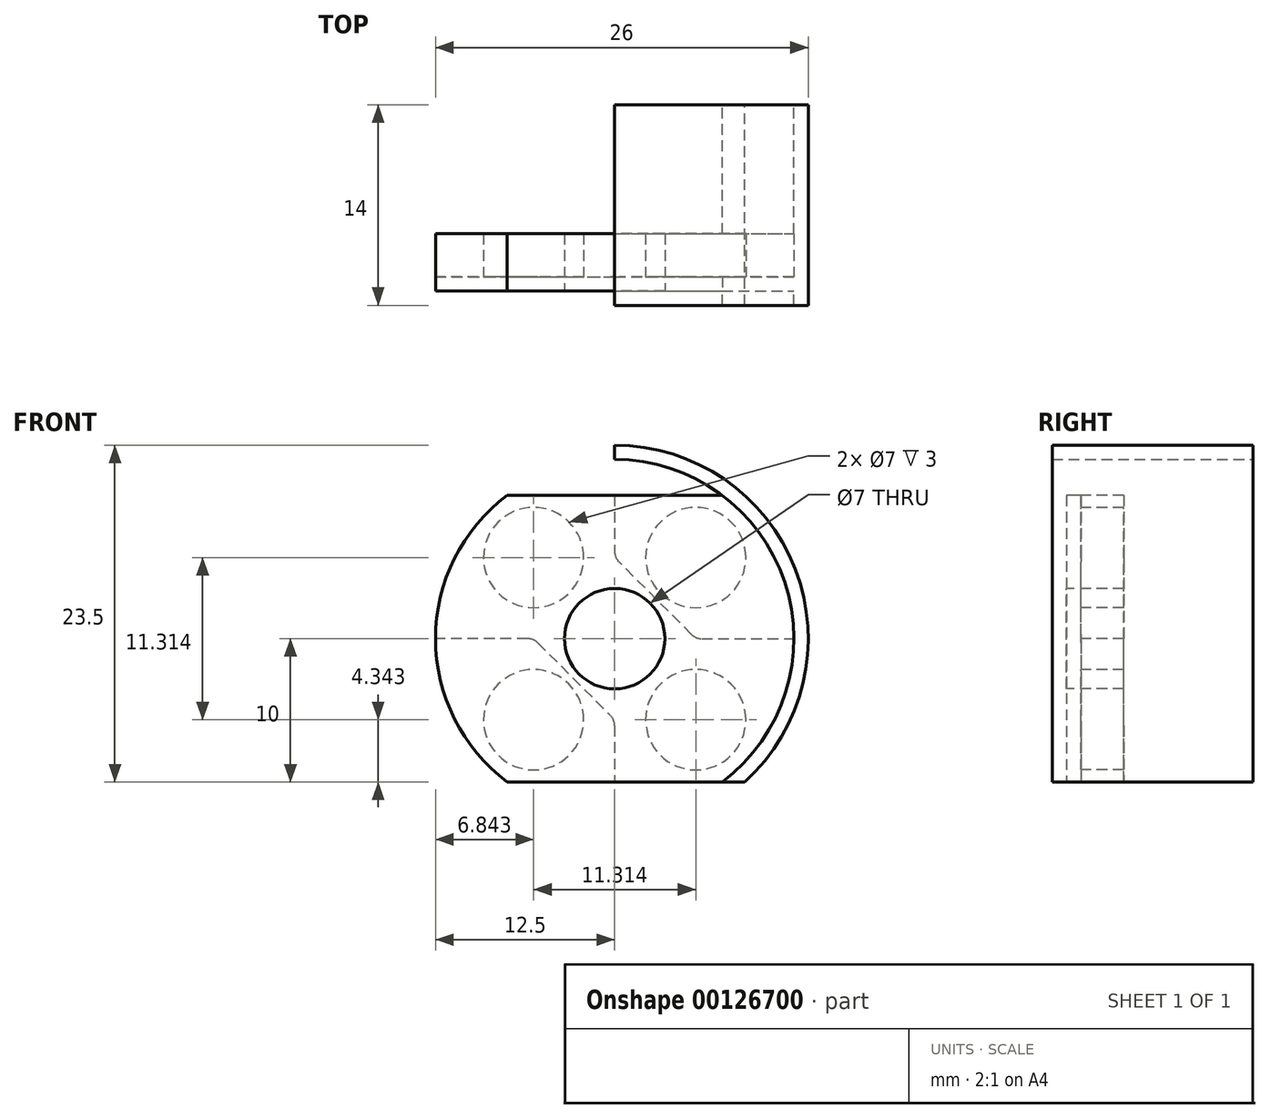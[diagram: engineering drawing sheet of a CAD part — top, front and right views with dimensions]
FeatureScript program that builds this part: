
annotation { "Feature Type Name" : "Feature", "Feature Type Description" : "" }
export const myFeature = defineFeature(function(context is Context, id is Id, definition is map)
    precondition{}
    {
        {
            var Q0;
            Q0=qCreatedBy(makeId("Front.planeOp"),FACE);
            var sketch = newSketch(context, id + "F0", { "sketchPlane" : qUnion([Q0])});
            skCircle(sketch, "E0", {"center": v(0, 0) * mm, "radius": 13.5 * mm});
            skLineSegment(sketch, "E1", {"start": v(0, 13.5) * mm, "end": v(0, 6.07) * mm});
            skLineSegment(sketch, "E2", {"start": v(6.07, 0) * mm, "end": v(13.5, 0) * mm});
            skCircle(sketch, "E3.0", {"center": v(0, 0) * mm, "radius": 12.5 * mm});
            skLineSegment(sketch, "E4", {"start": v(-8.84, 8.84) * mm, "end": v(8.84, -8.84) * mm});
            skCircle(sketch, "E5", {"center": v(0, 0) * mm, "radius": 3.5 * mm});
            skCircle(sketch, "E6", {"center": v(-5.66, 5.66) * mm, "radius": 3.5 * mm});
            skCircle(sketch, "E7", {"center": v(5.66, -5.66) * mm, "radius": 3.5 * mm});
            skCircle(sketch, "E8.MirrorC", {"center": v(5.66, 5.66) * mm, "radius": 3.5 * mm});
            skCircle(sketch, "E9.MirrorC", {"center": v(-5.66, -5.66) * mm, "radius": 3.5 * mm});
            skPoint(sketch, "E10", {"position": v(-2.83, 2.83) * mm});
            skLineSegment(sketch, "E11", {"start": v(-0.3, 5.36) * mm, "end": v(-5.36, 0.3) * mm});
            skLineSegment(sketch, "E12.MirrorCS", {"start": v(0.3, 5.36) * mm, "end": v(5.36, 0.3) * mm});
            skLineSegment(sketch, "E13.MirrorCS", {"start": v(0.3, -5.36) * mm, "end": v(5.36, -0.3) * mm});
            skLineSegment(sketch, "E14.MirrorCS", {"start": v(-0.3, -5.36) * mm, "end": v(-5.36, -0.3) * mm});
            skPoint(sketch, "E15.newPointA", {"position": v(0, 5.66) * mm});
            skArc(sketch, "E15.filletArc", {"start": v(-0.3, 5.36) * mm, "mid": v(-0.08, 5.69) * mm, "end": v(0, 6.07) * mm});
            skArc(sketch, "E16.filletArc", {"start": v(0, 6.07) * mm, "mid": v(0.08, 5.69) * mm, "end": v(0.3, 5.36) * mm});
            skPoint(sketch, "E17.newPointA", {"position": v(-13.5, 0) * mm});
            skPoint(sketch, "E17.newPointB", {"position": v(5.66, 0) * mm});
            skArc(sketch, "E17.filletArc", {"start": v(5.36, 0.3) * mm, "mid": v(5.69, 0.08) * mm, "end": v(6.07, 0) * mm});
            skArc(sketch, "E18.filletArc", {"start": v(6.07, 0) * mm, "mid": v(5.69, -0.08) * mm, "end": v(5.36, -0.3) * mm});
            skLineSegment(sketch, "E19", {"start": v(0, -6.07) * mm, "end": v(0, -12.5) * mm});
            skLineSegment(sketch, "E20", {"start": v(-6.07, 0) * mm, "end": v(-12.5, 0) * mm});
            skPoint(sketch, "E21.visualSharp", {"position": v(0, -5.66) * mm});
            skArc(sketch, "E21.filletArc", {"start": v(0.3, -5.36) * mm, "mid": v(0.08, -5.69) * mm, "end": v(0, -6.07) * mm});
            skArc(sketch, "E22.filletArc", {"start": v(0, -6.07) * mm, "mid": v(-0.08, -5.69) * mm, "end": v(-0.3, -5.36) * mm});
            skPoint(sketch, "E23.visualSharp", {"position": v(-5.66, 0) * mm});
            skArc(sketch, "E23.filletArc", {"start": v(-5.36, -0.3) * mm, "mid": v(-5.69, -0.08) * mm, "end": v(-6.07, 0) * mm});
            skArc(sketch, "E24.filletArc", {"start": v(-6.07, 0) * mm, "mid": v(-5.69, 0.08) * mm, "end": v(-5.36, 0.3) * mm});
            skLineSegment(sketch, "E25", {"start": v(-9.07, 10) * mm, "end": v(9.07, 10) * mm});
            skLineSegment(sketch, "E26", {"start": v(-9.07, -10) * mm, "end": v(9.07, -10) * mm});
            skSolve(sketch);
        }
        {
            var Q0;
            Q0=makeQuery(id+"F2.opExtrude","CAP_FACE",FACE,{"disambiguationData":[OSD([sQuery(id+"F0.wireOp",EDGE,"E0"),sQuery(id+"F0.wireOp",EDGE,"E3.0"),sQuery(id+"F0.wireOp",EDGE,"E25")])],"isStart":false});
            var Q1;
            {var subQ5=sQuery(id+"F0.wireOp",EDGE,"E15.filletArc");Q1=makeQuery(id+"F0.imprint","IMPRINT",FACE,{"disambiguationData":[TD([[makeQuery(id+"F0.imprint","IMPRINT",EDGE,{"derivedFrom":subQ5}),1.0]])]});}
            var Q2;
            Q2=makeQuery(id+"F0.imprint","IMPRINT",FACE,{"disambiguationData":[TD([[makeQuery(id+"F0.imprint","IMPRINT",EDGE,{"derivedFrom":sQuery(id+"F0.wireOp",EDGE,"E12.MirrorCS")}),-1.0]])]});
            var Q3;
            Q3=makeQuery(id+"F0.imprint","IMPRINT",FACE,{"disambiguationData":[TD([[makeQuery(id+"F0.imprint","IMPRINT",EDGE,{"derivedFrom":sQuery(id+"F0.wireOp",EDGE,"E14.MirrorCS")}),-1.0]])]});
            var Q4;
            Q4=makeQuery(id+"F0.imprint","IMPRINT",FACE,{"disambiguationData":[TD([[makeQuery(id+"F0.imprint","IMPRINT",EDGE,{"derivedFrom":sQuery(id+"F0.wireOp",EDGE,"E9.MirrorC")}),1.0]])]});
            var Q5;
            {var subQ10=sQuery(id+"F0.wireOp",EDGE,"E18.filletArc");Q5=makeQuery(id+"F0.imprint","IMPRINT",FACE,{"disambiguationData":[TD([[makeQuery(id+"F0.imprint","IMPRINT",EDGE,{"derivedFrom":subQ10}),1.0]])]});}
            var Q6;
            {var subQ12=sQuery(id+"F0.wireOp",EDGE,"E21.filletArc");Q6=makeQuery(id+"F0.imprint","IMPRINT",FACE,{"disambiguationData":[TD([[makeQuery(id+"F0.imprint","IMPRINT",EDGE,{"derivedFrom":subQ12}),1.0]])]});}
            var Q7;
            Q7=makeQuery(id+"F0.imprint","IMPRINT",FACE,{"disambiguationData":[TD([[makeQuery(id+"F0.imprint","IMPRINT",EDGE,{"derivedFrom":sQuery(id+"F0.wireOp",EDGE,"E8.MirrorC")}),1.0]])]});
            var Q8;
            {var subQ9=sQuery(id+"F0.wireOp",EDGE,"E20");Q8=makeQuery(id+"F0.imprint","IMPRINT",FACE,{"disambiguationData":[TD([[makeQuery(id+"F0.imprint","IMPRINT",EDGE,{"derivedFrom":subQ9}),-1.0]])]});}
            extrude(context, id + "F1", {"entities" : qUnion([Q0, Q1, Q2, Q3, Q4, Q5, Q6, Q7, Q8]), "oppositeDirection" : true, "depth" : 4 * mm});
        }
        {
            var Q0;
            {var subQ10=sQuery(id+"F0.wireOp",EDGE,"E2");var subQ11=sQuery(id+"F0.wireOp",EDGE,"E0");var subQ12=makeQuery(id+"F0.imprint","INTERSECT",VERTEX,{"derivedFrom":[subQ11,subQ10]});Q0=makeQuery(id+"F0.imprint","IMPRINT",FACE,{"disambiguationData":[TD([[makeQuery(id+"F0.imprint","IMPRINT",EDGE,{"disambiguationData":[TD([[subQ12,1.0]])],"derivedFrom":subQ11}),1.0]])]});}
            var Q1;
            {var subQ0=sQuery(id+"F0.wireOp",EDGE,"E2");var subQ1=sQuery(id+"F0.wireOp",EDGE,"E0");var subQ2=makeQuery(id+"F0.imprint","INTERSECT",VERTEX,{"derivedFrom":[subQ1,subQ0]});Q1=makeQuery(id+"F0.imprint","IMPRINT",FACE,{"disambiguationData":[TD([[makeQuery(id+"F0.imprint","IMPRINT",EDGE,{"disambiguationData":[TD([[subQ2,-1.0]])],"derivedFrom":subQ1}),1.0]])]});}
            var Q2;
            {var subQ3=sQuery(id+"F0.wireOp",EDGE,"E25");var subQ7=sQuery(id+"F0.wireOp",EDGE,"E0");var subQ8=makeQuery(id+"F0.imprint","INTERSECT",VERTEX,{"disambiguationData":[OD(0.0)],"derivedFrom":[subQ7,subQ3]});Q2=makeQuery(id+"F0.imprint","IMPRINT",FACE,{"disambiguationData":[TD([[makeQuery(id+"F0.imprint","IMPRINT",EDGE,{"disambiguationData":[TD([[subQ8,-1.0]])],"derivedFrom":subQ7}),1.0]])]});}
            extrude(context, id + "F2", {"entities" : qUnion([Q0, Q1, Q2]), "operationType" : NewBodyOperationType.ADD, "depth" : 1 * mm});
        }
        {
            var Q0;
            {var subQ0=sQuery(id+"F0.wireOp",EDGE,"E6");var subQ1=sQuery(id+"F0.wireOp",EDGE,"E4");var subQ2=makeQuery(id+"F0.imprint","INTERSECT",VERTEX,{"disambiguationData":[OD(0.0)],"derivedFrom":[subQ1,subQ0]});Q0=makeQuery(id+"F0.imprint","IMPRINT",FACE,{"disambiguationData":[TD([[makeQuery(id+"F0.imprint","IMPRINT",EDGE,{"disambiguationData":[TD([[subQ2,-1.0]])],"derivedFrom":subQ1}),-1.0]])]});}
            var Q1;
            {var subQ0=sQuery(id+"F0.wireOp",EDGE,"E6");var subQ1=sQuery(id+"F0.wireOp",EDGE,"E4");var subQ2=makeQuery(id+"F0.imprint","INTERSECT",VERTEX,{"disambiguationData":[OD(0.0)],"derivedFrom":[subQ1,subQ0]});Q1=makeQuery(id+"F0.imprint","IMPRINT",FACE,{"disambiguationData":[TD([[makeQuery(id+"F0.imprint","IMPRINT",EDGE,{"disambiguationData":[TD([[subQ2,-1.0]])],"derivedFrom":subQ1}),1.0]])]});}
            var Q2;
            Q2=makeQuery(id+"F0.imprint","IMPRINT",FACE,{"disambiguationData":[TD([[makeQuery(id+"F0.imprint","IMPRINT",EDGE,{"derivedFrom":sQuery(id+"F0.wireOp",EDGE,"E8.MirrorC")}),-1.0]])]});
            var Q3;
            {var subQ0=sQuery(id+"F0.wireOp",EDGE,"E5");var subQ1=sQuery(id+"F0.wireOp",EDGE,"E4");var subQ2=makeQuery(id+"F0.imprint","INTERSECT",VERTEX,{"disambiguationData":[OD(0.0)],"derivedFrom":[subQ1,subQ0]});Q3=makeQuery(id+"F0.imprint","IMPRINT",FACE,{"disambiguationData":[TD([[makeQuery(id+"F0.imprint","IMPRINT",EDGE,{"disambiguationData":[TD([[subQ2,-1.0]])],"derivedFrom":subQ1}),1.0]])]});}
            var Q4;
            {var subQ0=sQuery(id+"F0.wireOp",EDGE,"E5");var subQ1=sQuery(id+"F0.wireOp",EDGE,"E4");var subQ2=makeQuery(id+"F0.imprint","INTERSECT",VERTEX,{"disambiguationData":[OD(0.0)],"derivedFrom":[subQ1,subQ0]});Q4=makeQuery(id+"F0.imprint","IMPRINT",FACE,{"disambiguationData":[TD([[makeQuery(id+"F0.imprint","IMPRINT",EDGE,{"disambiguationData":[TD([[subQ2,-1.0]])],"derivedFrom":subQ1}),-1.0]])]});}
            var Q5;
            Q5=makeQuery(id+"F0.imprint","IMPRINT",FACE,{"disambiguationData":[TD([[makeQuery(id+"F0.imprint","IMPRINT",EDGE,{"derivedFrom":sQuery(id+"F0.wireOp",EDGE,"E9.MirrorC")}),-1.0]])]});
            var Q6;
            {var subQ0=sQuery(id+"F0.wireOp",EDGE,"E7");var subQ1=sQuery(id+"F0.wireOp",EDGE,"E4");var subQ2=makeQuery(id+"F0.imprint","INTERSECT",VERTEX,{"disambiguationData":[OD(0.0)],"derivedFrom":[subQ1,subQ0]});Q6=makeQuery(id+"F0.imprint","IMPRINT",FACE,{"disambiguationData":[TD([[makeQuery(id+"F0.imprint","IMPRINT",EDGE,{"disambiguationData":[TD([[subQ2,-1.0]])],"derivedFrom":subQ1}),1.0]])]});}
            var Q7;
            {var subQ0=sQuery(id+"F0.wireOp",EDGE,"E7");var subQ1=sQuery(id+"F0.wireOp",EDGE,"E4");var subQ2=makeQuery(id+"F0.imprint","INTERSECT",VERTEX,{"disambiguationData":[OD(0.0)],"derivedFrom":[subQ1,subQ0]});Q7=makeQuery(id+"F0.imprint","IMPRINT",FACE,{"disambiguationData":[TD([[makeQuery(id+"F0.imprint","IMPRINT",EDGE,{"disambiguationData":[TD([[subQ2,-1.0]])],"derivedFrom":subQ1}),-1.0]])]});}
            extrude(context, id + "F3", {"entities" : qUnion([Q0, Q1, Q2, Q3, Q4, Q5, Q6, Q7]), "operationType" : NewBodyOperationType.ADD, "oppositeDirection" : true, "depth" : 1 * mm});
        }
        {
            var Q0;
            {var subQ3=sQuery(id+"F0.wireOp",EDGE,"E25");var subQ7=sQuery(id+"F0.wireOp",EDGE,"E0");var subQ8=makeQuery(id+"F0.imprint","INTERSECT",VERTEX,{"disambiguationData":[OD(0.0)],"derivedFrom":[subQ7,subQ3]});Q0=makeQuery(id+"F0.imprint","IMPRINT",FACE,{"disambiguationData":[TD([[makeQuery(id+"F0.imprint","IMPRINT",EDGE,{"disambiguationData":[TD([[subQ8,-1.0]])],"derivedFrom":subQ7}),1.0]])]});}
            var Q1;
            {var subQ0=sQuery(id+"F0.wireOp",EDGE,"E2");var subQ1=sQuery(id+"F0.wireOp",EDGE,"E0");var subQ2=makeQuery(id+"F0.imprint","INTERSECT",VERTEX,{"derivedFrom":[subQ1,subQ0]});Q1=makeQuery(id+"F0.imprint","IMPRINT",FACE,{"disambiguationData":[TD([[makeQuery(id+"F0.imprint","IMPRINT",EDGE,{"disambiguationData":[TD([[subQ2,1.0]])],"derivedFrom":subQ1}),1.0]])]});}
            var Q2;
            {var subQ0=sQuery(id+"F0.wireOp",EDGE,"E2");var subQ1=sQuery(id+"F0.wireOp",EDGE,"E0");var subQ2=makeQuery(id+"F0.imprint","INTERSECT",VERTEX,{"derivedFrom":[subQ1,subQ0]});Q2=makeQuery(id+"F0.imprint","IMPRINT",FACE,{"disambiguationData":[TD([[makeQuery(id+"F0.imprint","IMPRINT",EDGE,{"disambiguationData":[TD([[subQ2,-1.0]])],"derivedFrom":subQ1}),1.0]])]});}
            extrude(context, id + "F4", {"entities" : qUnion([Q0, Q1, Q2]), "operationType" : NewBodyOperationType.ADD, "oppositeDirection" : true, "depth" : 13 * mm});
        }
    });
